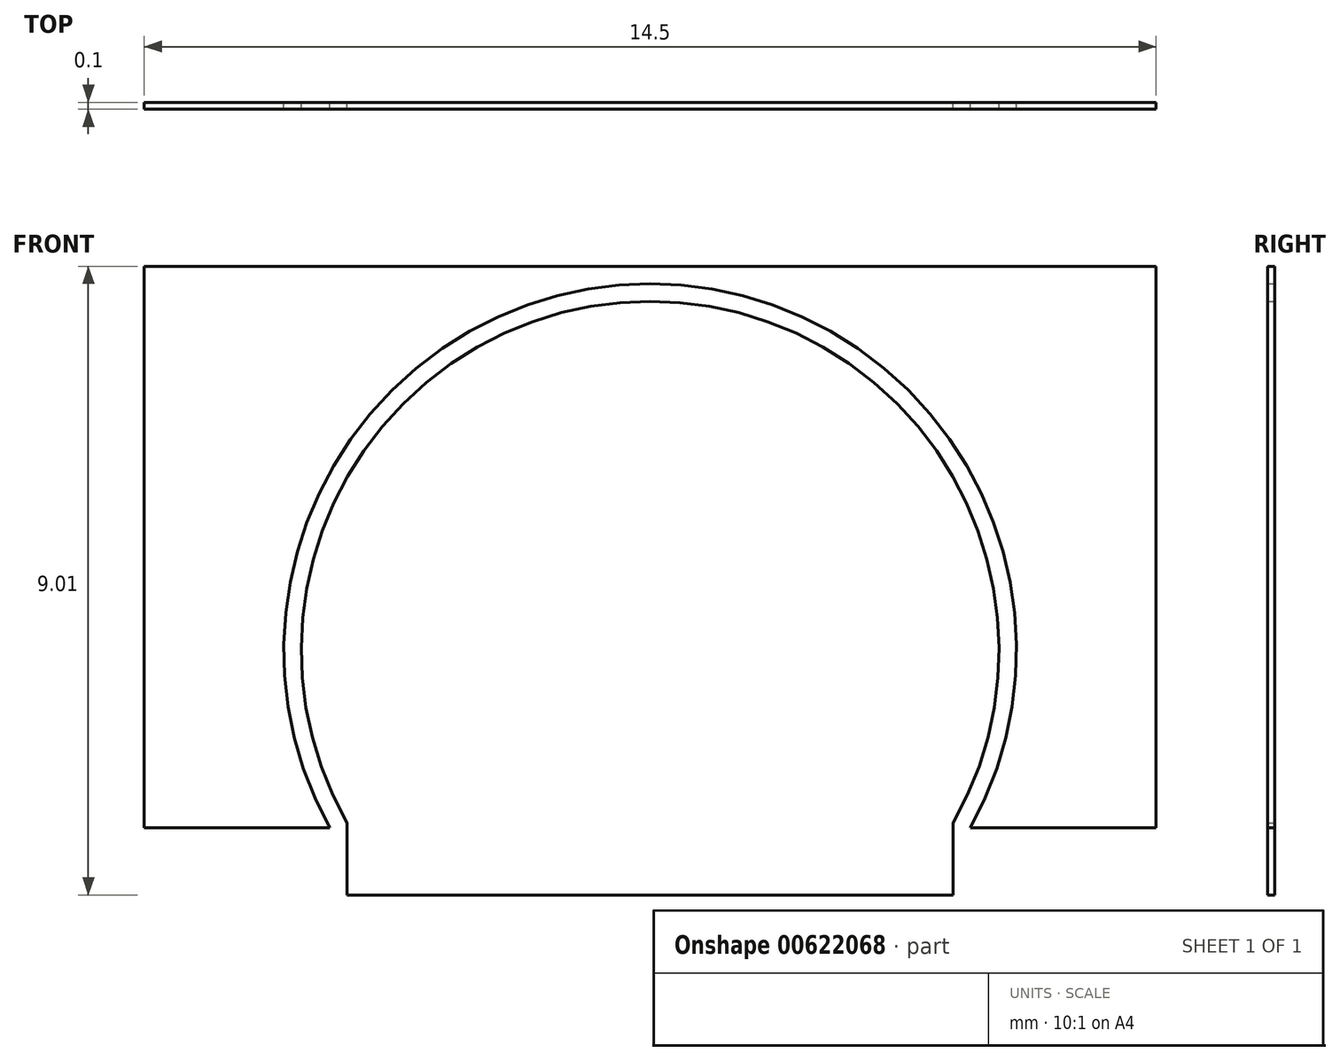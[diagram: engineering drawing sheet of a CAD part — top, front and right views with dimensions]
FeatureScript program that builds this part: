
annotation { "Feature Type Name" : "Feature", "Feature Type Description" : "" }
export const myFeature = defineFeature(function(context is Context, id is Id, definition is map)
    precondition{}
    {
        {
            var Q0;
            Q0=qCreatedBy(makeId("Front.planeOp"),FACE);
            var sketch = newSketch(context, id + "F0", { "sketchPlane" : qUnion([Q0])});
            skLineSegment(sketch, "E0", {"start": v(-4.34, 0) * mm, "end": v(-4.34, 1.03) * mm});
            skLineSegment(sketch, "E1", {"start": v(4.34, 1.03) * mm, "end": v(4.34, 0) * mm});
            skLineSegment(sketch, "E2", {"start": v(4.34, 0) * mm, "end": v(-4.34, 0) * mm});
            skArc(sketch, "E3", {"start": v(-4.34, 1.03) * mm, "mid": v(0, -1.5) * mm, "end": v(4.34, 1.03) * mm, "construction": true});
            skArc(sketch, "E4", {"start": v(4.34, 1.03) * mm, "mid": v(0, 8.5) * mm, "end": v(-4.34, 1.03) * mm});
            skLineSegment(sketch, "E5.bottom", {"start": v(-7.25, 0) * mm, "end": v(-4.34, 0) * mm, "construction": true});
            skLineSegment(sketch, "E5.top", {"start": v(-7.25, 9) * mm, "end": v(7.25, 9) * mm});
            skLineSegment(sketch, "E5.left", {"start": v(-7.25, 0) * mm, "end": v(-7.25, 0.96) * mm, "construction": true});
            skLineSegment(sketch, "E5.right", {"start": v(7.25, 0) * mm, "end": v(7.25, 0.96) * mm, "construction": true});
            skLineSegment(sketch, "E6.2", {"start": v(-4.6, 0) * mm, "end": v(-4.6, 0.96) * mm, "construction": true});
            skLineSegment(sketch, "E7", {"start": v(4.6, 0.96) * mm, "end": v(7.25, 0.96) * mm});
            skLineSegment(sketch, "E8", {"start": v(-4.6, 0.96) * mm, "end": v(-7.25, 0.96) * mm});
            skArc(sketch, "E9", {"start": v(4.6, 0.96) * mm, "mid": v(0, 8.76) * mm, "end": v(-4.6, 0.96) * mm});
            skLineSegment(sketch, "E10", {"start": v(7.25, 0.96) * mm, "end": v(7.25, 9) * mm});
            skLineSegment(sketch, "E11", {"start": v(4.34, 0) * mm, "end": v(7.25, 0) * mm, "construction": true});
            skLineSegment(sketch, "E12", {"start": v(-4.34, 0) * mm, "end": v(4.34, 0) * mm});
            skLineSegment(sketch, "E13", {"start": v(-7.25, 0.96) * mm, "end": v(-7.25, 9) * mm});
            skSolve(sketch);
        }
        {
            var Q0;
            Q0=makeQuery(id+"F0.imprint","IMPRINT",FACE,{"disambiguationData":[TD([[makeQuery(id+"F0.imprint","IMPRINT",EDGE,{"derivedFrom":sQuery(id+"F0.wireOp",EDGE,"E5.top")}),-1.0]])]});
            var Q1;
            Q1=makeQuery(id+"F0.imprint","IMPRINT",FACE,{"disambiguationData":[TD([[makeQuery(id+"F0.imprint","IMPRINT",EDGE,{"derivedFrom":sQuery(id+"F0.wireOp",EDGE,"E0")}),-1.0]])]});
            var Q2;
            Q2=sQuery(id+"F0.wireOp",EDGE,"E5.top");
            var Q3;
            Q3=sQuery(id+"F0.wireOp",EDGE,"E13");
            var Q4;
            Q4=sQuery(id+"F0.wireOp",EDGE,"E8");
            var Q5;
            Q5=sQuery(id+"F0.wireOp",EDGE,"E9");
            var Q6;
            Q6=sQuery(id+"F0.wireOp",EDGE,"E7");
            var Q7;
            Q7=sQuery(id+"F0.wireOp",EDGE,"E10");
            extrude(context, id + "F1", {"entities" : qUnion([Q0, Q1]), "surfaceEntities" : qUnion([Q2, Q3, Q4, Q5, Q6, Q7]), "depth" : 0.1 * mm, "offsetDistance" : 25 * mm});
        }
    });
